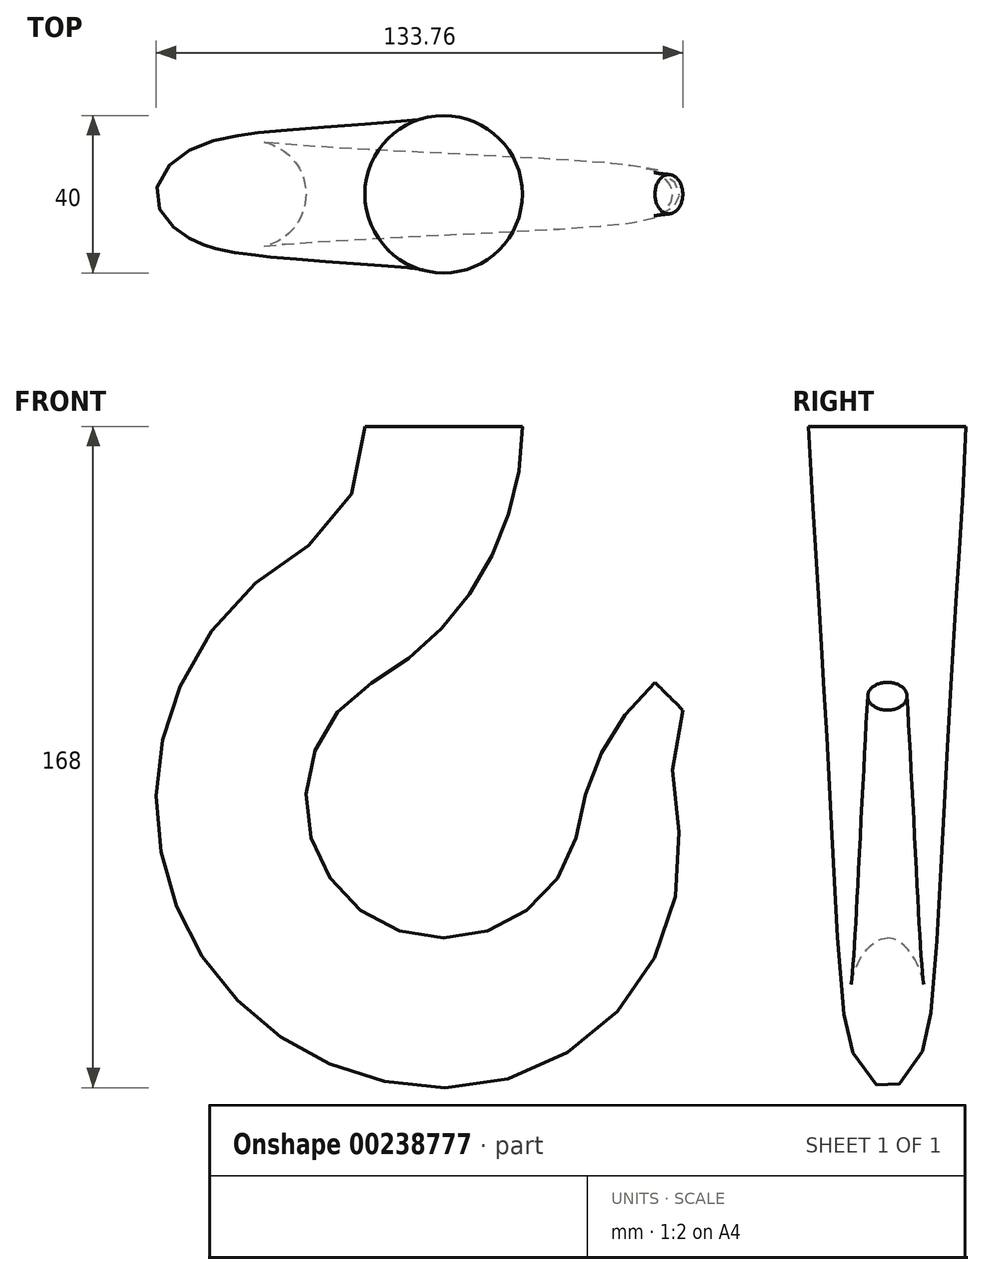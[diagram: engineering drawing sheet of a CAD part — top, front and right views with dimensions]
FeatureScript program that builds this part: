
annotation { "Feature Type Name" : "Feature", "Feature Type Description" : "" }
export const myFeature = defineFeature(function(context is Context, id is Id, definition is map)
    precondition{}
    {
        {
            var Q0;
            Q0=qCreatedBy(makeId("Front.planeOp"),FACE);
            var sketch = newSketch(context, id + "F0", { "sketchPlane" : qUnion([Q0])});
            skLineSegment(sketch, "E0", {"start": v(0, 95) * mm, "end": v(0, -73) * mm, "construction": true});
            skLineSegment(sketch, "E1.0", {"start": v(20, 95) * mm, "end": v(-20, 95) * mm});
            skArc(sketch, "E2", {"start": v(-17.5, 30.31) * mm, "mid": v(-20.02, -28.7) * mm, "end": v(34.5, -5.95) * mm});
            skArc(sketch, "E3.trimOffspring", {"start": v(-37.14, 62.85) * mm, "mid": v(-64.2, 34.75) * mm, "end": v(-72.93, -3.28) * mm});
            skArc(sketch, "E4", {"start": v(-72.93, -3.28) * mm, "mid": v(-50.45, -52.77) * mm, "end": v(0, -73) * mm});
            skArc(sketch, "E5", {"start": v(0, -73) * mm, "mid": v(46.12, -51.37) * mm, "end": v(59, -2.08) * mm});
            skArc(sketch, "E6", {"start": v(59, -2.08) * mm, "mid": v(58.29, 10.53) * mm, "end": v(60.76, 22.92) * mm});
            skArc(sketch, "E7", {"start": v(53.7, 30) * mm, "mid": v(40.95, 13.7) * mm, "end": v(34.5, -5.95) * mm});
            skLineSegment(sketch, "E8", {"start": v(53.7, 30) * mm, "end": v(60.76, 22.92) * mm});
            skPoint(sketch, "E9", {"position": v(0, -35) * mm});
            skArc(sketch, "E10", {"start": v(-37.14, 62.85) * mm, "mid": v(-24.05, 76.52) * mm, "end": v(-20, 95) * mm});
            skArc(sketch, "E11", {"start": v(-17.5, 30.31) * mm, "mid": v(9.89, 57.65) * mm, "end": v(20, 95) * mm});
            skLineSegment(sketch, "E12", {"start": v(-37.14, 62.85) * mm, "end": v(-17.5, 30.31) * mm});
            skSolve(sketch);
        }
        {
            var Q0;
            Q0=sQuery(id+"F0.wireOp",EDGE,"E12");
            cPlane(context, id + "F1", {"entities" : qUnion([Q0]), "cplaneType" : CPlaneType.LINE_ANGLE, "offset" : 25 * mm, "angle" : 0 * degree, "width" : 150 * mm, "height" : 150 * mm});
        }
        {
            var Q0;
            Q0=sQuery(id+"F0.wireOp",EDGE,"E1.0");
            cPlane(context, id + "F2", {"entities" : qUnion([Q0]), "cplaneType" : CPlaneType.LINE_ANGLE, "offset" : 25 * mm, "angle" : 90 * degree, "width" : 150 * mm, "height" : 150 * mm});
        }
        {
            var Q0;
            Q0=qCreatedBy(id+"F2.planeOp",FACE);
            var sketch = newSketch(context, id + "F3", { "sketchPlane" : qUnion([Q0])});
            skCircle(sketch, "E13", {"center": v(0, 0) * mm, "radius": 20 * mm});
            skSolve(sketch);
        }
        {
            var Q0;
            Q0=sQuery(id+"F0.wireOp",EDGE,"E8");
            cPlane(context, id + "F4", {"entities" : qUnion([Q0]), "cplaneType" : CPlaneType.LINE_ANGLE, "offset" : 25 * mm, "angle" : 90 * degree, "width" : 150 * mm, "height" : 150 * mm});
        }
        {
            var Q0;
            Q0=qCreatedBy(id+"F4.planeOp",FACE);
            var sketch = newSketch(context, id + "F5", { "sketchPlane" : qUnion([Q0])});
            skPoint(sketch, "E14.first.point", {"position": v(0, -16.7) * mm});
            skPoint(sketch, "E14.second.point", {"position": v(0, -26.67) * mm});
            skLineSegment(sketch, "E15.0", {"start": v(0, -16.67) * mm, "end": v(0, -26.67) * mm});
            skCircle(sketch, "E16", {"center": v(0, -21.67) * mm, "radius": 5 * mm});
            skSolve(sketch);
        }
        {
            var Q0;
            Q0=qCreatedBy(makeId("Front.planeOp"),FACE);
            var sketch = newSketch(context, id + "F6", { "sketchPlane" : qUnion([Q0])});
            skArc(sketch, "E17.0", {"start": v(-17.5, 30.31) * mm, "mid": v(9.89, 57.65) * mm, "end": v(20, 95) * mm});
            skArc(sketch, "E18.0", {"start": v(-17.5, 30.31) * mm, "mid": v(-20.02, -28.7) * mm, "end": v(34.5, -5.95) * mm});
            skArc(sketch, "E19.0", {"start": v(53.7, 30) * mm, "mid": v(40.95, 13.7) * mm, "end": v(34.5, -5.95) * mm});
            skSolve(sketch);
        }
        {
            var Q0;
            Q0=qCreatedBy(makeId("Front.planeOp"),FACE);
            var sketch = newSketch(context, id + "F7", { "sketchPlane" : qUnion([Q0])});
            skArc(sketch, "E20.0", {"start": v(-37.14, 62.85) * mm, "mid": v(-24.05, 76.52) * mm, "end": v(-20, 95) * mm});
            skArc(sketch, "E21.0", {"start": v(-37.14, 62.85) * mm, "mid": v(-64.2, 34.75) * mm, "end": v(-72.93, -3.28) * mm});
            skArc(sketch, "E22.0", {"start": v(-72.93, -3.28) * mm, "mid": v(-50.45, -52.77) * mm, "end": v(0, -73) * mm});
            skArc(sketch, "E23.0", {"start": v(0, -73) * mm, "mid": v(46.12, -51.37) * mm, "end": v(59, -2.08) * mm});
            skPoint(sketch, "E24.0", {"position": v(58.29, 10.53) * mm});
            skArc(sketch, "E25.0", {"start": v(59, -2.08) * mm, "mid": v(58.29, 10.53) * mm, "end": v(60.76, 22.92) * mm});
            skSolve(sketch);
        }
        {
            var Q0;
            Q0=makeQuery(id+"F3.imprint","IMPRINT",FACE,{"disambiguationData":[TD([[makeQuery(id+"F3.imprint","IMPRINT",EDGE,{"derivedFrom":sQuery(id+"F3.wireOp",EDGE,"E13")}),1.0]])]});
            var Q1;
            Q1 = qSketchRegion(id + "F5", true);
            var Q2;
            Q2 = qConstructionFilter(qBodyType(qCreatedBy(id + "F6" ,EDGE), BodyType.WIRE), ConstructionObject.NO);
            var Q3;
            Q3 = qConstructionFilter(qBodyType(qCreatedBy(id + "F7" ,EDGE), BodyType.WIRE), ConstructionObject.NO);
            loft(context, id + "F8", {"addGuides" : true, "sheetProfilesArray" : [{ "sheetProfileEntities" : qUnion([Q0]) }, { "sheetProfileEntities" : qUnion([Q1]) }], "guidesArray" : [{ "guideEntities" : qUnion([Q2]), "guideDerivativeType" : LoftGuideDerivativeType.DEFAULT, "guideDerivativeMagnitude" : 1 }, { "guideEntities" : qUnion([Q3]), "guideDerivativeType" : LoftGuideDerivativeType.DEFAULT, "guideDerivativeMagnitude" : 1 }]});
        }
    });
